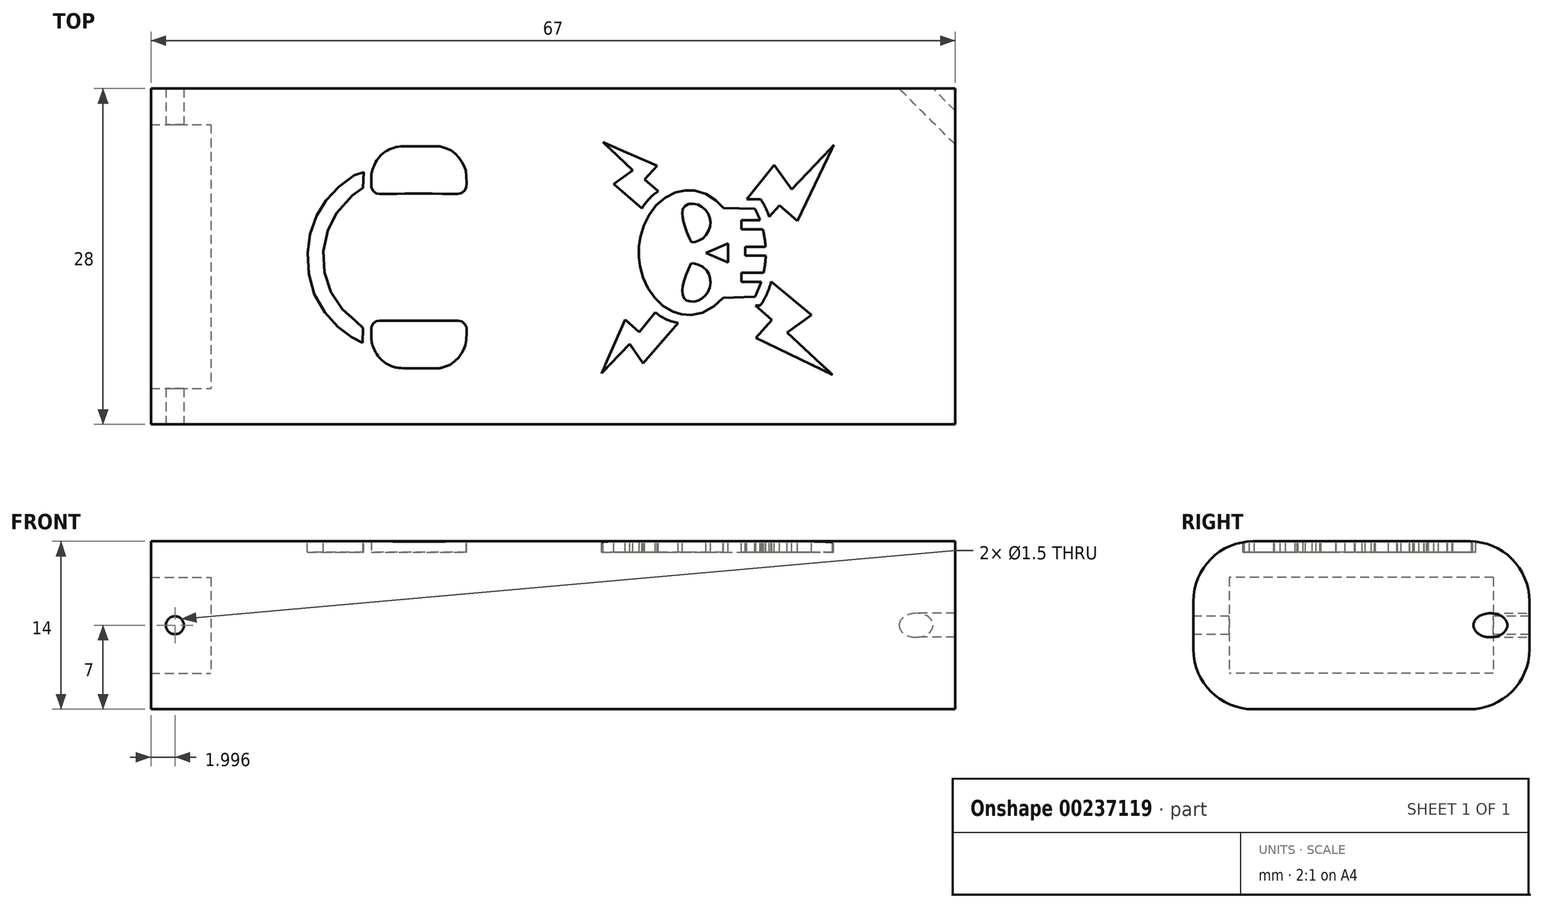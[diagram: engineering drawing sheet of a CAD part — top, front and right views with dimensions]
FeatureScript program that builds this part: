
annotation { "Feature Type Name" : "Feature", "Feature Type Description" : "" }
export const myFeature = defineFeature(function(context is Context, id is Id, definition is map)
    precondition{}
    {
        {
            var Q0;
            Q0=qCreatedBy(makeId("Top.planeOp"),FACE);
            var sketch = newSketch(context, id + "F0", { "sketchPlane" : qUnion([Q0])});
            skLineSegment(sketch, "E0.bottom", {"start": v(-10.86, 8.8) * mm, "end": v(49.14, 8.8) * mm});
            skLineSegment(sketch, "E0.top", {"start": v(-10.86, -13.2) * mm, "end": v(49.14, -13.2) * mm});
            skLineSegment(sketch, "E0.left", {"start": v(-10.86, 8.8) * mm, "end": v(-10.86, -13.2) * mm});
            skLineSegment(sketch, "E0.right", {"start": v(49.14, 8.8) * mm, "end": v(49.14, -13.2) * mm});
            skSolve(sketch);
        }
        {
            var Q0;
            Q0=makeQuery(id+"F0.imprint","IMPRINT",FACE,{"disambiguationData":[TD([[makeQuery(id+"F0.imprint","IMPRINT",EDGE,{"derivedFrom":sQuery(id+"F0.wireOp",EDGE,"E0.bottom")}),-1.0]])]});
            extrude(context, id + "F1", {"entities" : qUnion([Q0]), "depth" : 8 * mm});
        }
        {
            var Q0;
            Q0=makeQuery(id+"F1.opExtrude","SWEPT_FACE",FACE,{"disambiguationData":[OSD([sQuery(id+"F0.wireOp",EDGE,"E0.right")])]});
            var sketch = newSketch(context, id + "F2", { "sketchPlane" : qUnion([Q0])});
            skLineSegment(sketch, "E1.0", {"start": v(8.8, 8) * mm, "end": v(8.8, 0) * mm});
            skLineSegment(sketch, "E1.1", {"start": v(8.8, 0) * mm, "end": v(-13.2, 0) * mm});
            skLineSegment(sketch, "E1.2", {"start": v(8.8, 8) * mm, "end": v(-13.2, 8) * mm});
            skLineSegment(sketch, "E1.3", {"start": v(-13.2, 8) * mm, "end": v(-13.2, 0) * mm});
            skLineSegment(sketch, "E2.0", {"start": v(11.8, 6) * mm, "end": v(11.8, 2) * mm});
            skLineSegment(sketch, "E2.1", {"start": v(6.8, 11) * mm, "end": v(-11.2, 11) * mm});
            skLineSegment(sketch, "E2.2", {"start": v(-16.2, 6) * mm, "end": v(-16.2, 2) * mm});
            skLineSegment(sketch, "E2.3", {"start": v(6.8, -3) * mm, "end": v(-11.2, -3) * mm});
            skPoint(sketch, "E3.visualSharp", {"position": v(11.8, 11) * mm});
            skArc(sketch, "E3.filletArc", {"start": v(11.8, 6) * mm, "mid": v(10.33, 9.54) * mm, "end": v(6.8, 11) * mm});
            skPoint(sketch, "E4.visualSharp", {"position": v(11.8, -3) * mm});
            skArc(sketch, "E4.filletArc", {"start": v(6.8, -3) * mm, "mid": v(10.33, -1.54) * mm, "end": v(11.8, 2) * mm});
            skPoint(sketch, "E5.visualSharp", {"position": v(-16.2, -3) * mm});
            skArc(sketch, "E5.filletArc", {"start": v(-16.2, 2) * mm, "mid": v(-14.74, -1.54) * mm, "end": v(-11.2, -3) * mm});
            skPoint(sketch, "E6.visualSharp", {"position": v(-16.2, 11) * mm});
            skArc(sketch, "E6.filletArc", {"start": v(-11.2, 11) * mm, "mid": v(-14.74, 9.54) * mm, "end": v(-16.2, 6) * mm});
            skSolve(sketch);
        }
        {
            var Q0;
            Q0 = qSketchRegion(id + "F2", true);
            extrude(context, id + "F3", {"entities" : qUnion([Q0]), "oppositeDirection" : true, "depth" : 65 * mm});
        }
        {
            var Q0;
            Q0=makeQuery(id+"F2.imprint","IMPRINT",FACE,{"disambiguationData":[TD([[makeQuery(id+"F2.imprint","IMPRINT",EDGE,{"derivedFrom":sQuery(id+"F2.wireOp",EDGE,"E1.0")}),1.0]])]});
            var Q1;
            Q1=makeQuery(id+"F2.imprint","IMPRINT",FACE,{"disambiguationData":[TD([[makeQuery(id+"F2.imprint","IMPRINT",EDGE,{"derivedFrom":sQuery(id+"F2.wireOp",EDGE,"E1.0")}),-1.0]])]});
            extrude(context, id + "F4", {"entities" : qUnion([Q0, Q1]), "operationType" : NewBodyOperationType.ADD, "depth" : 2 * mm});
        }
        {
            var Q0;
            {var subQ0=sQuery(id+"F2.wireOp",EDGE,"E2.1");Q0=makeQuery(id+"F4.boolean.opBoolean","MERGE",FACE,{"derivedFrom":[makeQuery(id+"F3.opExtrude","SWEPT_FACE",FACE,{"disambiguationData":[OSD([subQ0])]}),makeQuery(id+"F4.opExtrude","SWEPT_FACE",FACE,{"disambiguationData":[OSD([subQ0])]})]});}
            var sketch = newSketch(context, id + "F5", { "sketchPlane" : qUnion([Q0])});
            skFitSpline(sketch, "E7", {"points": [v(1.77, -9.41) * mm, v(1.8, -8.72) * mm, v(1.78, -8.01) * mm, v(1.67, -7.93) * mm, v(1.1, -7.53) * mm, v(0.3, -6.83) * mm, v(-0.5, -5.83) * mm, v(-1.23, -4.28) * mm, v(-1.49, -2.91) * mm, v(-1.44, -1.17) * mm, v(-1.03, 0.28) * mm, v(-0.39, 1.44) * mm, v(0.9, 2.86) * mm, v(1.68, 3.4) * mm, v(1.81, 3.52) * mm, v(1.84, 4.23) * mm, v(1.81, 4.93) * mm, v(1.62, 4.88) * mm, v(0.85, 4.43) * mm, v(-0.19, 3.64) * mm, v(-1.07, 2.73) * mm, v(-1.69, 1.86) * mm, v(-2.31, 0.62) * mm, v(-2.67, -0.62) * mm, v(-2.81, -1.82) * mm, v(-2.76, -3.4) * mm, v(-2.42, -4.88) * mm, v(-1.77, -6.3) * mm, v(-0.8, -7.55) * mm, v(0, -8.33) * mm, v(0.85, -8.92) * mm, v(1.48, -9.32) * mm, v(1.77, -9.41) * mm]});
            skFitSpline(sketch, "E8", {"points": [v(2.51, -8.1) * mm, v(2.5, -8.5) * mm, v(2.5, -9.15) * mm, v(2.56, -9.49) * mm, v(2.73, -9.94) * mm, v(3.04, -10.49) * mm, v(3.64, -11.07) * mm, v(4.34, -11.4) * mm, v(4.6, -11.47) * mm, v(4.86, -11.5) * mm, v(5.11, -11.52) * mm, v(5.86, -11.53) * mm, v(6.7, -11.53) * mm, v(7.6, -11.53) * mm, v(7.99, -11.54) * mm, v(8.15, -11.53) * mm, v(8.42, -11.46) * mm, v(8.63, -11.4) * mm, v(8.83, -11.33) * mm, v(9.06, -11.22) * mm, v(9.33, -11.04) * mm, v(9.54, -10.85) * mm, v(9.76, -10.63) * mm, v(9.95, -10.36) * mm, v(10.1, -10.12) * mm, v(10.2, -9.9) * mm, v(10.29, -9.71) * mm, v(10.36, -9.52) * mm, v(10.4, -9.33) * mm, v(10.42, -8.8) * mm, v(10.43, -8.37) * mm, v(10.42, -8.13) * mm, v(10.4, -8.02) * mm, v(10.3, -7.87) * mm, v(10.17, -7.74) * mm, v(10.04, -7.63) * mm, v(9.88, -7.58) * mm, v(9.74, -7.57) * mm, v(9.3, -7.57) * mm, v(8.6, -7.57) * mm, v(7.65, -7.57) * mm, v(6.6, -7.57) * mm, v(5.48, -7.57) * mm, v(4.75, -7.57) * mm, v(3.9, -7.57) * mm, v(3.16, -7.57) * mm, v(3.05, -7.57) * mm, v(2.92, -7.6) * mm, v(2.78, -7.67) * mm, v(2.66, -7.78) * mm, v(2.57, -7.93) * mm, v(2.51, -8.1) * mm]});
            skFitSpline(sketch, "E9.MirrorC", {"points": [v(2.51, 3.56) * mm, v(2.5, 3.95) * mm, v(2.5, 4.6) * mm, v(2.56, 4.94) * mm, v(2.73, 5.4) * mm, v(3.04, 5.94) * mm, v(3.64, 6.52) * mm, v(4.34, 6.86) * mm, v(4.6, 6.92) * mm, v(4.86, 6.96) * mm, v(5.11, 6.97) * mm, v(5.86, 6.98) * mm, v(6.7, 6.98) * mm, v(7.6, 6.98) * mm, v(7.99, 6.99) * mm, v(8.15, 6.98) * mm, v(8.42, 6.91) * mm, v(8.63, 6.85) * mm, v(8.83, 6.78) * mm, v(9.06, 6.67) * mm, v(9.33, 6.5) * mm, v(9.54, 6.3) * mm, v(9.76, 6.08) * mm, v(9.95, 5.81) * mm, v(10.1, 5.57) * mm, v(10.2, 5.36) * mm, v(10.29, 5.16) * mm, v(10.36, 4.97) * mm, v(10.4, 4.78) * mm, v(10.42, 4.26) * mm, v(10.43, 3.82) * mm, v(10.42, 3.58) * mm, v(10.4, 3.47) * mm, v(10.3, 3.33) * mm, v(10.17, 3.2) * mm, v(10.04, 3.08) * mm, v(9.88, 3.04) * mm, v(9.74, 3.03) * mm, v(9.3, 3.02) * mm, v(8.6, 3.02) * mm, v(7.65, 3.03) * mm, v(5.48, 3.03) * mm, v(4.75, 3.03) * mm, v(3.9, 3.02) * mm, v(3.16, 3.02) * mm, v(3.05, 3.02) * mm, v(2.92, 3.04) * mm, v(2.78, 3.12) * mm, v(2.66, 3.23) * mm, v(2.57, 3.38) * mm, v(2.51, 3.56) * mm]});
            skLineSegment(sketch, "E10", {"start": v(21.68, -11.94) * mm, "end": v(23.65, -7.48) * mm});
            skLineSegment(sketch, "E11", {"start": v(23.65, -7.48) * mm, "end": v(24.8, -8.51) * mm});
            skLineSegment(sketch, "E12", {"start": v(24.8, -8.51) * mm, "end": v(26.15, -6.86) * mm});
            skLineSegment(sketch, "E13", {"start": v(21.68, -11.94) * mm, "end": v(24.02, -9.5) * mm});
            skLineSegment(sketch, "E14", {"start": v(24.02, -9.5) * mm, "end": v(25.15, -11.13) * mm});
            skLineSegment(sketch, "E15", {"start": v(25.15, -11.13) * mm, "end": v(28.07, -7.74) * mm});
            skLineSegment(sketch, "E16", {"start": v(25.04, 1.8) * mm, "end": v(22.7, 3.82) * mm});
            skLineSegment(sketch, "E17", {"start": v(22.7, 3.82) * mm, "end": v(24.28, 4.97) * mm});
            skLineSegment(sketch, "E18", {"start": v(24.28, 4.97) * mm, "end": v(21.82, 7.31) * mm});
            skLineSegment(sketch, "E19", {"start": v(21.82, 7.31) * mm, "end": v(26.32, 5.35) * mm});
            skLineSegment(sketch, "E20", {"start": v(26.32, 5.35) * mm, "end": v(25.25, 4.2) * mm});
            skLineSegment(sketch, "E21", {"start": v(25.25, 4.2) * mm, "end": v(26.41, 3.24) * mm});
            skLineSegment(sketch, "E22", {"start": v(35.64, 1.1) * mm, "end": v(36.5, 2.07) * mm});
            skLineSegment(sketch, "E23", {"start": v(36.5, 2.07) * mm, "end": v(38, 0.75) * mm});
            skLineSegment(sketch, "E24", {"start": v(38, 0.75) * mm, "end": v(41.02, 7.06) * mm});
            skLineSegment(sketch, "E25", {"start": v(41.02, 7.06) * mm, "end": v(37.53, 3.38) * mm});
            skLineSegment(sketch, "E26", {"start": v(37.53, 3.38) * mm, "end": v(36.05, 5.4) * mm});
            skLineSegment(sketch, "E27", {"start": v(36.05, 5.4) * mm, "end": v(33.77, 2.58) * mm});
            skLineSegment(sketch, "E28", {"start": v(33.77, 2.58) * mm, "end": v(34.91, 2.58) * mm});
            skLineSegment(sketch, "E29", {"start": v(34.91, -6.29) * mm, "end": v(34.51, -6.29) * mm});
            skLineSegment(sketch, "E30", {"start": v(34.51, -6.29) * mm, "end": v(35.87, -7.5) * mm});
            skLineSegment(sketch, "E31", {"start": v(35.87, -7.5) * mm, "end": v(34.54, -8.98) * mm});
            skLineSegment(sketch, "E32", {"start": v(34.54, -8.98) * mm, "end": v(40.92, -12.07) * mm});
            skLineSegment(sketch, "E33", {"start": v(40.92, -12.07) * mm, "end": v(37.15, -8.53) * mm});
            skLineSegment(sketch, "E34", {"start": v(37.15, -8.53) * mm, "end": v(39.17, -7.07) * mm});
            skLineSegment(sketch, "E35", {"start": v(39.17, -7.07) * mm, "end": v(35.8, -4.3) * mm});
            skLineSegment(sketch, "E36", {"start": v(30.38, -1.9) * mm, "end": v(32.22, -2.71) * mm});
            skLineSegment(sketch, "E37", {"start": v(32.22, -2.71) * mm, "end": v(32.22, -1.13) * mm});
            skLineSegment(sketch, "E38", {"start": v(32.22, -1.13) * mm, "end": v(30.38, -1.9) * mm});
            skLineSegment(sketch, "E39", {"start": v(31.8, -5.65) * mm, "end": v(34.45, -5.57) * mm});
            skLineSegment(sketch, "E40", {"start": v(31.83, 1.84) * mm, "end": v(34.45, 1.79) * mm});
            skLineSegment(sketch, "E41", {"start": v(34.88, 0.82) * mm, "end": v(33.34, 0.82) * mm});
            skLineSegment(sketch, "E42", {"start": v(33.34, 0.82) * mm, "end": v(33.34, 0.06) * mm});
            skLineSegment(sketch, "E43", {"start": v(33.34, 0.06) * mm, "end": v(35.11, 0.06) * mm});
            skLineSegment(sketch, "E44", {"start": v(35.34, -1.4) * mm, "end": v(33.66, -1.4) * mm});
            skLineSegment(sketch, "E45", {"start": v(33.66, -1.4) * mm, "end": v(33.66, -2.14) * mm});
            skLineSegment(sketch, "E46", {"start": v(33.66, -2.14) * mm, "end": v(35.36, -2.14) * mm});
            skLineSegment(sketch, "E47", {"start": v(35.18, -3.57) * mm, "end": v(33.34, -3.57) * mm});
            skLineSegment(sketch, "E48", {"start": v(33.34, -3.57) * mm, "end": v(33.34, -4.33) * mm});
            skLineSegment(sketch, "E49", {"start": v(33.34, -4.33) * mm, "end": v(34.97, -4.33) * mm});
            skFitSpline(sketch, "E50", {"points": [v(31.8, -5.65) * mm, v(31.6, -5.88) * mm, v(31.2, -6.23) * mm, v(30.76, -6.54) * mm, v(30.35, -6.78) * mm, v(29.9, -6.95) * mm, v(29.49, -7.05) * mm, v(29.2, -7.08) * mm, v(28.93, -7.08) * mm, v(28.64, -7.07) * mm, v(28.37, -7.04) * mm, v(28.22, -7.01) * mm, v(27.95, -6.93) * mm, v(27.7, -6.84) * mm, v(27.46, -6.72) * mm, v(27.08, -6.53) * mm, v(26.8, -6.33) * mm, v(26.48, -6.06) * mm, v(26.24, -5.8) * mm, v(26.03, -5.56) * mm, v(25.78, -5.23) * mm, v(25.54, -4.86) * mm, v(25.37, -4.5) * mm, v(25.22, -4.16) * mm, v(25.09, -3.83) * mm, v(25, -3.45) * mm, v(24.89, -3.04) * mm, v(24.84, -2.76) * mm, v(24.8, -2.53) * mm, v(24.8, -2.3) * mm, v(24.78, -2.06) * mm, v(24.78, -1.66) * mm, v(24.79, -1.37) * mm, v(24.82, -1.09) * mm, v(24.85, -0.83) * mm, v(24.92, -0.53) * mm, v(25.01, -0.12) * mm, v(25.14, 0.26) * mm, v(25.3, 0.64) * mm, v(25.49, 1.03) * mm, v(25.68, 1.35) * mm, v(25.93, 1.72) * mm, v(26.17, 2) * mm, v(26.45, 2.27) * mm, v(26.72, 2.5) * mm, v(27.08, 2.76) * mm, v(27.4, 2.96) * mm, v(27.78, 3.13) * mm, v(28.13, 3.23) * mm, v(28.39, 3.28) * mm, v(28.55, 3.3) * mm, v(28.78, 3.32) * mm, v(29.06, 3.32) * mm, v(29.35, 3.3) * mm, v(29.63, 3.27) * mm, v(30.01, 3.15) * mm, v(30.43, 2.97) * mm, v(30.77, 2.79) * mm, v(31.12, 2.54) * mm, v(31.44, 2.27) * mm, v(31.67, 2.03) * mm, v(31.83, 1.84) * mm], "startDerivative": vector(-11.4, -13.93) * mm, "endDerivative": vector(11.21, -13.36) * mm});
            skFitSpline(sketch, "E51", {"points": [v(29.15, -2.78) * mm, v(28.98, -3.1) * mm, v(28.82, -3.47) * mm, v(28.7, -3.77) * mm, v(28.6, -4.05) * mm, v(28.52, -4.34) * mm, v(28.45, -4.66) * mm, v(28.42, -4.88) * mm, v(28.4, -5.06) * mm, v(28.4, -5.21) * mm, v(28.42, -5.33) * mm, v(28.44, -5.46) * mm, v(28.48, -5.58) * mm, v(28.55, -5.7) * mm, v(28.62, -5.78) * mm, v(28.72, -5.85) * mm, v(28.83, -5.9) * mm, v(29, -5.95) * mm, v(29.12, -5.96) * mm, v(29.26, -5.97) * mm, v(29.37, -5.97) * mm, v(29.57, -5.94) * mm, v(29.7, -5.89) * mm, v(29.86, -5.81) * mm, v(29.99, -5.74) * mm, v(30.1, -5.66) * mm, v(30.25, -5.54) * mm, v(30.37, -5.4) * mm, v(30.5, -5.25) * mm, v(30.6, -5.06) * mm, v(30.69, -4.84) * mm, v(30.74, -4.64) * mm, v(30.76, -4.47) * mm, v(30.76, -4.27) * mm, v(30.74, -4.12) * mm, v(30.71, -3.97) * mm, v(30.65, -3.77) * mm, v(30.56, -3.59) * mm, v(30.47, -3.42) * mm, v(30.3, -3.23) * mm, v(30.1, -3.07) * mm, v(29.91, -2.96) * mm, v(29.73, -2.89) * mm, v(29.57, -2.83) * mm, v(29.45, -2.8) * mm, v(29.33, -2.78) * mm, v(29.22, -2.77) * mm, v(29.15, -2.78) * mm]});
            skFitSpline(sketch, "E52", {"points": [v(29.17, -1) * mm, v(29.04, -0.79) * mm, v(28.95, -0.56) * mm, v(28.8, -0.23) * mm, v(28.69, 0.1) * mm, v(28.56, 0.44) * mm, v(28.5, 0.67) * mm, v(28.45, 0.9) * mm, v(28.42, 1.08) * mm, v(28.4, 1.24) * mm, v(28.4, 1.45) * mm, v(28.41, 1.62) * mm, v(28.44, 1.76) * mm, v(28.53, 1.88) * mm, v(28.65, 2.02) * mm, v(28.82, 2.15) * mm, v(28.98, 2.19) * mm, v(29.17, 2.2) * mm, v(29.41, 2.18) * mm, v(29.6, 2.15) * mm, v(29.79, 2.1) * mm, v(29.97, 1.99) * mm, v(30.22, 1.81) * mm, v(30.36, 1.66) * mm, v(30.5, 1.47) * mm, v(30.6, 1.3) * mm, v(30.68, 1.1) * mm, v(30.72, 0.91) * mm, v(30.75, 0.76) * mm, v(30.76, 0.58) * mm, v(30.75, 0.39) * mm, v(30.7, 0.2) * mm, v(30.63, 0) * mm, v(30.53, -0.2) * mm, v(30.35, -0.45) * mm, v(30.2, -0.61) * mm, v(30.07, -0.73) * mm, v(29.96, -0.8) * mm, v(29.75, -0.9) * mm, v(29.6, -0.96) * mm, v(29.4, -1) * mm, v(29.23, -1.02) * mm, v(29.17, -1) * mm]});
            skArc(sketch, "E53", {"start": v(26.41, 3.24) * mm, "mid": v(25.64, 2.6) * mm, "end": v(25.04, 1.8) * mm});
            skArc(sketch, "E54", {"start": v(35.64, 1.1) * mm, "mid": v(35.34, 1.87) * mm, "end": v(34.91, 2.58) * mm});
            skArc(sketch, "E55", {"start": v(34.45, -5.57) * mm, "mid": v(34.74, -4.96) * mm, "end": v(34.97, -4.33) * mm});
            skArc(sketch, "E56.trimOffspring", {"start": v(35.18, -3.57) * mm, "mid": v(35.3, -2.86) * mm, "end": v(35.36, -2.14) * mm});
            skArc(sketch, "E57.trimOffspring", {"start": v(35.34, -1.4) * mm, "mid": v(35.26, -0.66) * mm, "end": v(35.11, 0.06) * mm});
            skArc(sketch, "E58.trimOffspring", {"start": v(34.88, 0.82) * mm, "mid": v(34.68, 1.3) * mm, "end": v(34.45, 1.79) * mm});
            skArc(sketch, "E59", {"start": v(34.91, -6.29) * mm, "mid": v(35.45, -5.34) * mm, "end": v(35.8, -4.3) * mm});
            skArc(sketch, "E60", {"start": v(26.15, -6.86) * mm, "mid": v(27.05, -7.44) * mm, "end": v(28.07, -7.74) * mm});
            skSolve(sketch);
        }
        {
            var Q0;
            {var subQ0=sQuery(id+"F5.wireOp",EDGE,"E9.MirrorC");var subQ1=sQuery(id+"F2.wireOp",EDGE,"E3.filletArc");var subQ2=sQuery(id+"F2.wireOp",EDGE,"E2.1");var subQ3=makeQuery(id+"F4.boolean.opBoolean","MERGE",EDGE,{"derivedFrom":[makeQuery(id+"F3.opExtrude","SWEPT_EDGE",EDGE,{"disambiguationData":[OSD([subQ2,subQ1])]}),makeQuery(id+"F4.opExtrude","SWEPT_EDGE",EDGE,{"disambiguationData":[OSD([subQ2,subQ1])]})]});var subQ4=makeQuery(id+"F5.imprint","INTERSECT",VERTEX,{"disambiguationData":[OD(0.0)],"derivedFrom":[subQ3,subQ0]});Q0=makeQuery(id+"F5.imprint","IMPRINT",FACE,{"disambiguationData":[TD([[makeQuery(id+"F5.imprint","IMPRINT",EDGE,{"disambiguationData":[TD([[subQ4,1.0]])],"derivedFrom":subQ0}),-1.0]])]});}
            var Q1;
            {var subQ0=sQuery(id+"F5.wireOp",EDGE,"E9.MirrorC");var subQ1=sQuery(id+"F2.wireOp",EDGE,"E3.filletArc");var subQ2=sQuery(id+"F2.wireOp",EDGE,"E2.1");var subQ3=makeQuery(id+"F4.boolean.opBoolean","MERGE",EDGE,{"derivedFrom":[makeQuery(id+"F3.opExtrude","SWEPT_EDGE",EDGE,{"disambiguationData":[OSD([subQ2,subQ1])]}),makeQuery(id+"F4.opExtrude","SWEPT_EDGE",EDGE,{"disambiguationData":[OSD([subQ2,subQ1])]})]});var subQ4=makeQuery(id+"F5.imprint","INTERSECT",VERTEX,{"disambiguationData":[OD(0.0)],"derivedFrom":[subQ3,subQ0]});Q1=makeQuery(id+"F5.imprint","IMPRINT",FACE,{"disambiguationData":[TD([[makeQuery(id+"F5.imprint","IMPRINT",EDGE,{"disambiguationData":[TD([[subQ4,-1.0]])],"derivedFrom":subQ0}),-1.0]])]});}
            var Q2;
            Q2=makeQuery(id+"F5.imprint","IMPRINT",FACE,{"disambiguationData":[TD([[makeQuery(id+"F5.imprint","IMPRINT",EDGE,{"derivedFrom":sQuery(id+"F5.wireOp",EDGE,"E7")}),1.0]])]});
            var Q3;
            {var subQ0=sQuery(id+"F5.wireOp",EDGE,"E8");var subQ1=sQuery(id+"F2.wireOp",EDGE,"E6.filletArc");var subQ2=sQuery(id+"F2.wireOp",EDGE,"E2.1");var subQ3=makeQuery(id+"F4.boolean.opBoolean","MERGE",EDGE,{"derivedFrom":[makeQuery(id+"F3.opExtrude","SWEPT_EDGE",EDGE,{"disambiguationData":[OSD([subQ2,subQ1])]}),makeQuery(id+"F4.opExtrude","SWEPT_EDGE",EDGE,{"disambiguationData":[OSD([subQ2,subQ1])]})]});var subQ4=makeQuery(id+"F5.imprint","INTERSECT",VERTEX,{"disambiguationData":[OD(0.0)],"derivedFrom":[subQ3,subQ0]});Q3=makeQuery(id+"F5.imprint","IMPRINT",FACE,{"disambiguationData":[TD([[makeQuery(id+"F5.imprint","IMPRINT",EDGE,{"disambiguationData":[TD([[subQ4,1.0]])],"derivedFrom":subQ0}),1.0]])]});}
            var Q4;
            {var subQ0=sQuery(id+"F5.wireOp",EDGE,"E8");var subQ1=sQuery(id+"F2.wireOp",EDGE,"E6.filletArc");var subQ2=sQuery(id+"F2.wireOp",EDGE,"E2.1");var subQ3=makeQuery(id+"F4.boolean.opBoolean","MERGE",EDGE,{"derivedFrom":[makeQuery(id+"F3.opExtrude","SWEPT_EDGE",EDGE,{"disambiguationData":[OSD([subQ2,subQ1])]}),makeQuery(id+"F4.opExtrude","SWEPT_EDGE",EDGE,{"disambiguationData":[OSD([subQ2,subQ1])]})]});var subQ4=makeQuery(id+"F5.imprint","INTERSECT",VERTEX,{"disambiguationData":[OD(0.0)],"derivedFrom":[subQ3,subQ0]});Q4=makeQuery(id+"F5.imprint","IMPRINT",FACE,{"disambiguationData":[TD([[makeQuery(id+"F5.imprint","IMPRINT",EDGE,{"disambiguationData":[TD([[subQ4,-1.0]])],"derivedFrom":subQ0}),1.0]])]});}
            var Q5;
            Q5=makeQuery(id+"F5.imprint","IMPRINT",FACE,{"disambiguationData":[TD([[makeQuery(id+"F5.imprint","IMPRINT",EDGE,{"derivedFrom":sQuery(id+"F5.wireOp",EDGE,"E36")}),-1.0]])]});
            var Q6;
            Q6=makeQuery(id+"F5.imprint","IMPRINT",FACE,{"disambiguationData":[TD([[makeQuery(id+"F5.imprint","IMPRINT",EDGE,{"derivedFrom":sQuery(id+"F5.wireOp",EDGE,"E16")}),-1.0]])]});
            var Q7;
            Q7=makeQuery(id+"F5.imprint","IMPRINT",FACE,{"disambiguationData":[TD([[makeQuery(id+"F5.imprint","IMPRINT",EDGE,{"derivedFrom":sQuery(id+"F5.wireOp",EDGE,"E22")}),1.0]])]});
            var Q8;
            Q8=makeQuery(id+"F5.imprint","IMPRINT",FACE,{"disambiguationData":[TD([[makeQuery(id+"F5.imprint","IMPRINT",EDGE,{"derivedFrom":sQuery(id+"F5.wireOp",EDGE,"E29")}),1.0]])]});
            var Q9;
            {var subQ0=sQuery(id+"F5.wireOp",EDGE,"E11");Q9=makeQuery(id+"F5.imprint","IMPRINT",FACE,{"disambiguationData":[TD([[makeQuery(id+"F5.imprint","IMPRINT",EDGE,{"derivedFrom":subQ0}),-1.0]])]});}
            var Q10;
            {var subQ0=sQuery(id+"F5.wireOp",EDGE,"E13");var subQ1=sQuery(id+"F5.wireOp",EDGE,"E10");var subQ2=makeQuery(id+"F5.imprint","INTERSECT",VERTEX,{"derivedFrom":[subQ1,subQ0]});Q10=makeQuery(id+"F5.imprint","IMPRINT",FACE,{"disambiguationData":[TD([[makeQuery(id+"F5.imprint","IMPRINT",EDGE,{"disambiguationData":[TD([[subQ2,-1.0]])],"derivedFrom":subQ1}),-1.0]])]});}
            var Q11;
            {var subQ0=sQuery(id+"F5.wireOp",EDGE,"E19");var subQ1=sQuery(id+"F5.wireOp",EDGE,"E18");var subQ2=makeQuery(id+"F5.imprint","INTERSECT",VERTEX,{"derivedFrom":[subQ1,subQ0]});Q11=makeQuery(id+"F5.imprint","IMPRINT",FACE,{"disambiguationData":[TD([[makeQuery(id+"F5.imprint","IMPRINT",EDGE,{"disambiguationData":[TD([[subQ2,1.0]])],"derivedFrom":subQ1}),-1.0]])]});}
            var Q12;
            {var subQ0=sQuery(id+"F5.wireOp",EDGE,"E33");var subQ1=sQuery(id+"F5.wireOp",EDGE,"E32");var subQ2=makeQuery(id+"F5.imprint","INTERSECT",VERTEX,{"derivedFrom":[subQ1,subQ0]});Q12=makeQuery(id+"F5.imprint","IMPRINT",FACE,{"disambiguationData":[TD([[makeQuery(id+"F5.imprint","IMPRINT",EDGE,{"disambiguationData":[TD([[subQ2,1.0]])],"derivedFrom":subQ1}),1.0]])]});}
            var Q13;
            {var subQ0=sQuery(id+"F5.wireOp",EDGE,"E25");var subQ1=sQuery(id+"F5.wireOp",EDGE,"E24");var subQ2=makeQuery(id+"F5.imprint","INTERSECT",VERTEX,{"derivedFrom":[subQ1,subQ0]});Q13=makeQuery(id+"F5.imprint","IMPRINT",FACE,{"disambiguationData":[TD([[makeQuery(id+"F5.imprint","IMPRINT",EDGE,{"disambiguationData":[TD([[subQ2,1.0]])],"derivedFrom":subQ1}),1.0]])]});}
            extrude(context, id + "F6", {"entities" : qUnion([Q0, Q1, Q2, Q3, Q4, Q5, Q6, Q7, Q8, Q9, Q10, Q11, Q12, Q13]), "operationType" : NewBodyOperationType.REMOVE, "oppositeDirection" : true, "depth" : 0.9 * mm});
        }
        {
            var Q0;
            {var subQ0=sQuery(id+"F2.wireOp",EDGE,"E2.2");Q0=makeQuery(id+"F4.boolean.opBoolean","MERGE",FACE,{"derivedFrom":[makeQuery(id+"F3.opExtrude","SWEPT_FACE",FACE,{"disambiguationData":[OSD([subQ0])]}),makeQuery(id+"F4.opExtrude","SWEPT_FACE",FACE,{"disambiguationData":[OSD([subQ0])]})]});}
            var sketch = newSketch(context, id + "F7", { "sketchPlane" : qUnion([Q0])});
            skCircle(sketch, "E61", {"center": v(-13.86, 4) * mm, "radius": 0.75 * mm});
            skPoint(sketch, "E61.centerSnap0", {"position": v(-15.86, 4) * mm});
            skSolve(sketch);
        }
        {
            var Q0;
            Q0 = qSketchRegion(id + "F7", true);
            extrude(context, id + "F8", {"entities" : qUnion([Q0]), "operationType" : NewBodyOperationType.REMOVE, "endBound" : BoundingType.THROUGH_ALL, "oppositeDirection" : true, "depth" : 25 * mm});
        }
        {
            var Q0;
            Q0=sQuery(id+"F2.wireOp",EDGE,"E1.0");
            cPlane(context, id + "F9", {"entities" : qUnion([Q0]), "cplaneType" : CPlaneType.LINE_ANGLE, "offset" : 25 * mm, "angle" : 45 * degree, "width" : 150 * mm, "height" : 150 * mm});
        }
        {
            var Q0;
            Q0=qCreatedBy(id+"F9.planeOp",FACE);
            var sketch = newSketch(context, id + "F10", { "sketchPlane" : qUnion([Q0])});
            skLineSegment(sketch, "E62.0", {"start": v(-44.5, 6) * mm, "end": v(-44.5, 2) * mm});
            skCircle(sketch, "E63", {"center": v(-42.2, 4) * mm, "radius": 1 * mm});
            skPoint(sketch, "E63.centerSnap0", {"position": v(-44.5, 4) * mm});
            skSolve(sketch);
        }
        {
            var Q0;
            Q0 = qSketchRegion(id + "F10", true);
            extrude(context, id + "F11", {"entities" : qUnion([Q0]), "operationType" : NewBodyOperationType.REMOVE, "endBound" : BoundingType.UP_TO_NEXT, "oppositeDirection" : true, "depth" : 25 * mm, "hasSecondDirection" : true, "secondDirectionBound" : SecondDirectionBoundingType.UP_TO_NEXT, "secondDirectionOppositeDirection" : false, "secondDirectionDepth" : 25 * mm});
        }
    });
